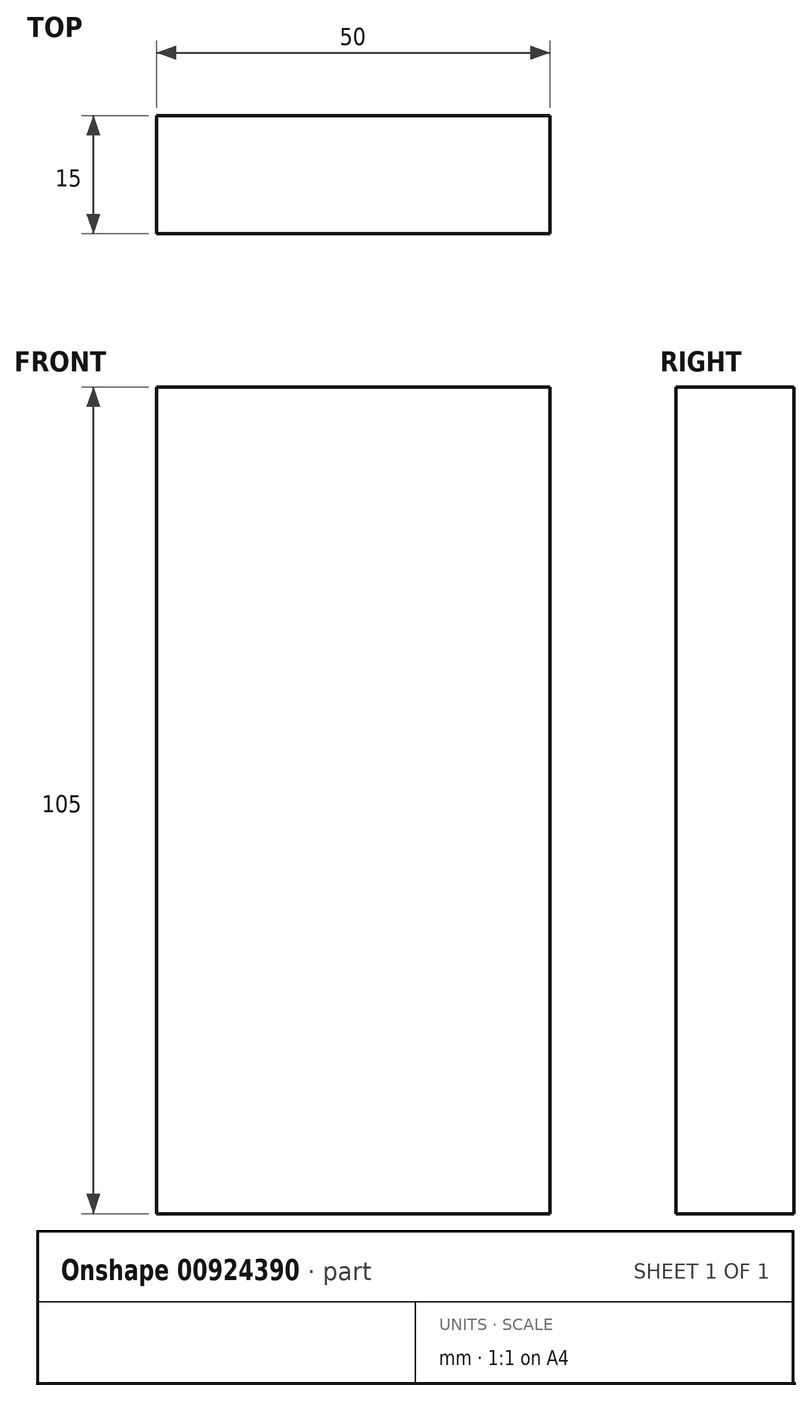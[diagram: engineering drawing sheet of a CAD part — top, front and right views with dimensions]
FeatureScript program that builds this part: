
annotation { "Feature Type Name" : "Feature", "Feature Type Description" : "" }
export const myFeature = defineFeature(function(context is Context, id is Id, definition is map)
    precondition{}
    {
        {
            var Q0;
            Q0=qCreatedBy(makeId("Front.planeOp"),FACE);
            var sketch = newSketch(context, id + "F0", { "sketchPlane" : qUnion([Q0])});
            skLineSegment(sketch, "E0.bottom", {"start": v(25, -52.5) * mm, "end": v(-25, -52.5) * mm});
            skLineSegment(sketch, "E0.top", {"start": v(25, 52.5) * mm, "end": v(-25, 52.5) * mm});
            skLineSegment(sketch, "E0.left", {"start": v(25, -52.5) * mm, "end": v(25, 52.5) * mm});
            skLineSegment(sketch, "E0.right", {"start": v(-25, -52.5) * mm, "end": v(-25, 52.5) * mm});
            skPoint(sketch, "E0.middle", {"position": v(0, 0) * mm});
            skSolve(sketch);
        }
        {
            var Q0;
            Q0 = qSketchRegion(id + "F0", true);
            extrude(context, id + "F1", {"entities" : qUnion([Q0]), "oppositeDirection" : true, "depth" : 15 * mm, "offsetDistance" : 25 * mm});
        }
    });
